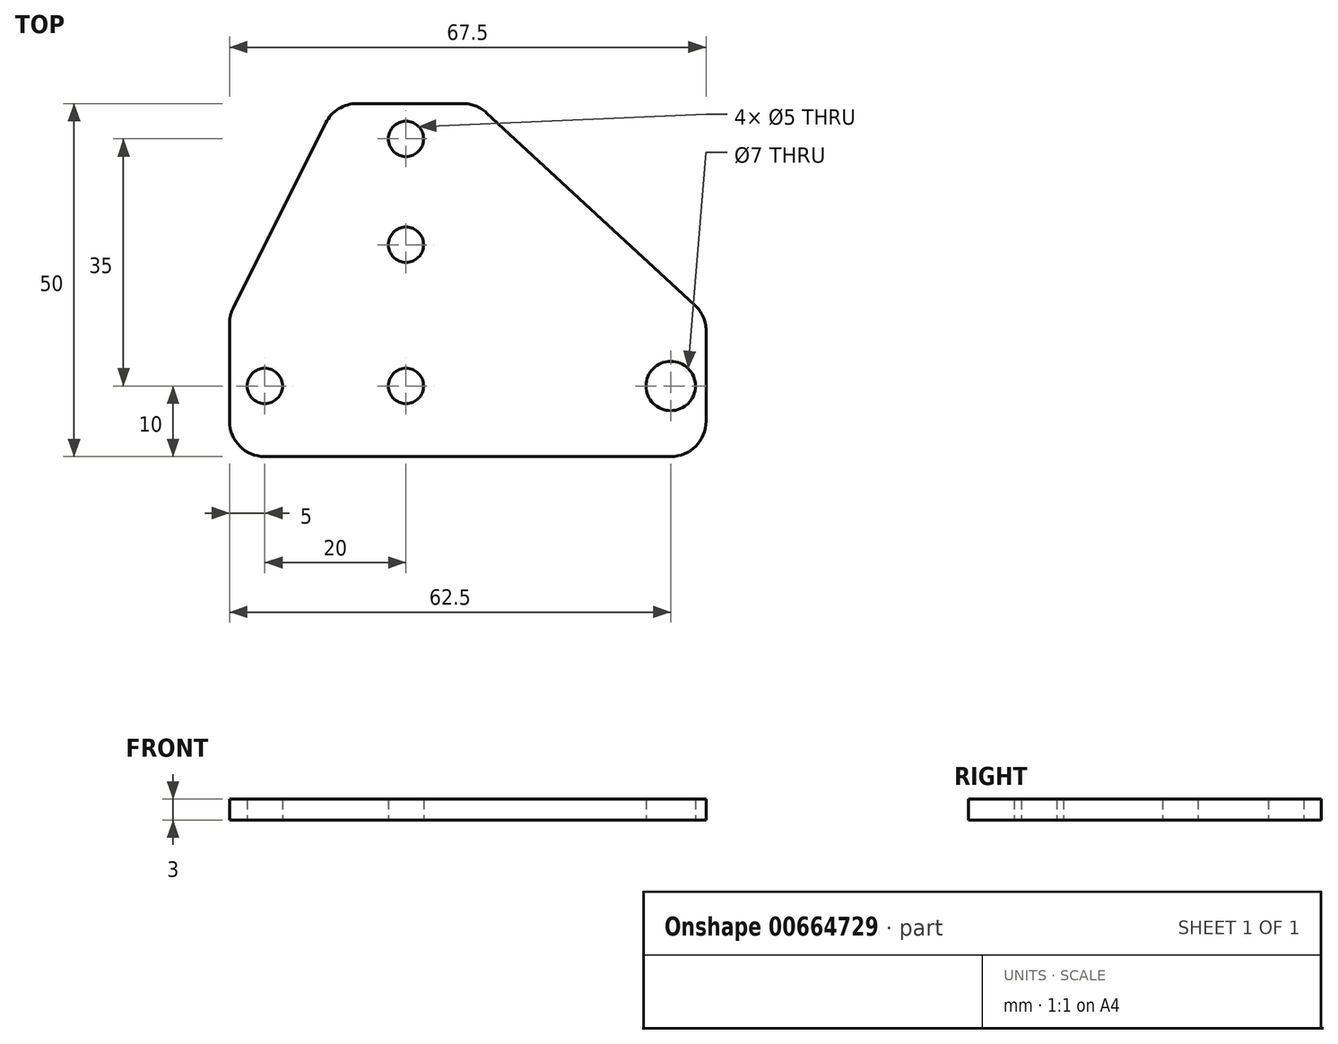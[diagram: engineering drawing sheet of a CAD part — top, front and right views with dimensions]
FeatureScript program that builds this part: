
annotation { "Feature Type Name" : "Feature", "Feature Type Description" : "" }
export const myFeature = defineFeature(function(context is Context, id is Id, definition is map)
    precondition{}
    {
        {
            var Q0;
            Q0=qCreatedBy(makeId("Top.planeOp"),FACE);
            var sketch = newSketch(context, id + "F0", { "sketchPlane" : qUnion([Q0])});
            skLineSegment(sketch, "E0", {"start": v(0, 5) * mm, "end": v(0, 18.82) * mm});
            skLineSegment(sketch, "E1", {"start": v(5, 0) * mm, "end": v(62.5, 0) * mm});
            skLineSegment(sketch, "E2.0", {"start": v(0, 10) * mm, "end": v(72.85, 10) * mm, "construction": true});
            skLineSegment(sketch, "E3.0", {"start": v(0, 20) * mm, "end": v(72.85, 20) * mm, "construction": true});
            skLineSegment(sketch, "E4.0", {"start": v(0, 30) * mm, "end": v(72.85, 30) * mm, "construction": true});
            skLineSegment(sketch, "E5.0", {"start": v(0, 45) * mm, "end": v(72.85, 45) * mm, "construction": true});
            skLineSegment(sketch, "E6.0", {"start": v(18.1, 50) * mm, "end": v(33.05, 50) * mm});
            skLineSegment(sketch, "E7.0", {"start": v(5, 0) * mm, "end": v(5, 53.67) * mm, "construction": true});
            skLineSegment(sketch, "E8.0", {"start": v(15, 0) * mm, "end": v(15, 53.67) * mm, "construction": true});
            skLineSegment(sketch, "E9.0", {"start": v(25, 0) * mm, "end": v(25, 53.67) * mm, "construction": true});
            skLineSegment(sketch, "E10.0", {"start": v(0, 25) * mm, "end": v(72.85, 25) * mm, "construction": true});
            skLineSegment(sketch, "E11.0", {"start": v(35, 0) * mm, "end": v(35, 53.67) * mm, "construction": true});
            skLineSegment(sketch, "E12.0", {"start": v(62.5, 0) * mm, "end": v(62.5, 53.67) * mm, "construction": true});
            skLineSegment(sketch, "E13.0", {"start": v(67.5, 5) * mm, "end": v(67.5, 17.81) * mm});
            skCircle(sketch, "E14", {"center": v(5, 10) * mm, "radius": 2.5 * mm});
            skCircle(sketch, "E15", {"center": v(62.5, 10) * mm, "radius": 3.5 * mm});
            skCircle(sketch, "E16", {"center": v(25, 10) * mm, "radius": 2.5 * mm});
            skCircle(sketch, "E17", {"center": v(25, 30) * mm, "radius": 2.5 * mm});
            skCircle(sketch, "E18", {"center": v(25, 45) * mm, "radius": 2.5 * mm});
            skLineSegment(sketch, "E19", {"start": v(0.53, 21.06) * mm, "end": v(13.62, 47.24) * mm});
            skLineSegment(sketch, "E20", {"start": v(36.44, 48.67) * mm, "end": v(65.9, 21.48) * mm});
            skArc(sketch, "E21.filletArc", {"start": v(18.1, 50) * mm, "mid": v(15.46, 49.25) * mm, "end": v(13.62, 47.24) * mm});
            skArc(sketch, "E22.filletArc", {"start": v(36.44, 48.67) * mm, "mid": v(34.87, 49.66) * mm, "end": v(33.05, 50) * mm});
            skArc(sketch, "E23.filletArc", {"start": v(67.5, 17.81) * mm, "mid": v(67.08, 19.82) * mm, "end": v(65.9, 21.48) * mm});
            skArc(sketch, "E24.filletArc", {"start": v(62.5, 0) * mm, "mid": v(66.04, 1.46) * mm, "end": v(67.5, 5) * mm});
            skPoint(sketch, "E25.visualSharp", {"position": v(0, 0) * mm});
            skArc(sketch, "E25.filletArc", {"start": v(0, 5) * mm, "mid": v(1.46, 1.46) * mm, "end": v(5, 0) * mm});
            skArc(sketch, "E26.filletArc", {"start": v(0.53, 21.06) * mm, "mid": v(0.13, 19.97) * mm, "end": v(0, 18.82) * mm});
            skSolve(sketch);
        }
        {
            var Q0;
            Q0=makeQuery(id+"F0.imprint","IMPRINT",FACE,{"disambiguationData":[TD([[makeQuery(id+"F0.imprint","IMPRINT",EDGE,{"derivedFrom":sQuery(id+"F0.wireOp",EDGE,"E14")}),-1.0]])]});
            extrude(context, id + "F1", {"entities" : qUnion([Q0]), "depth" : 3 * mm, "offsetDistance" : 25 * mm});
        }
    });
